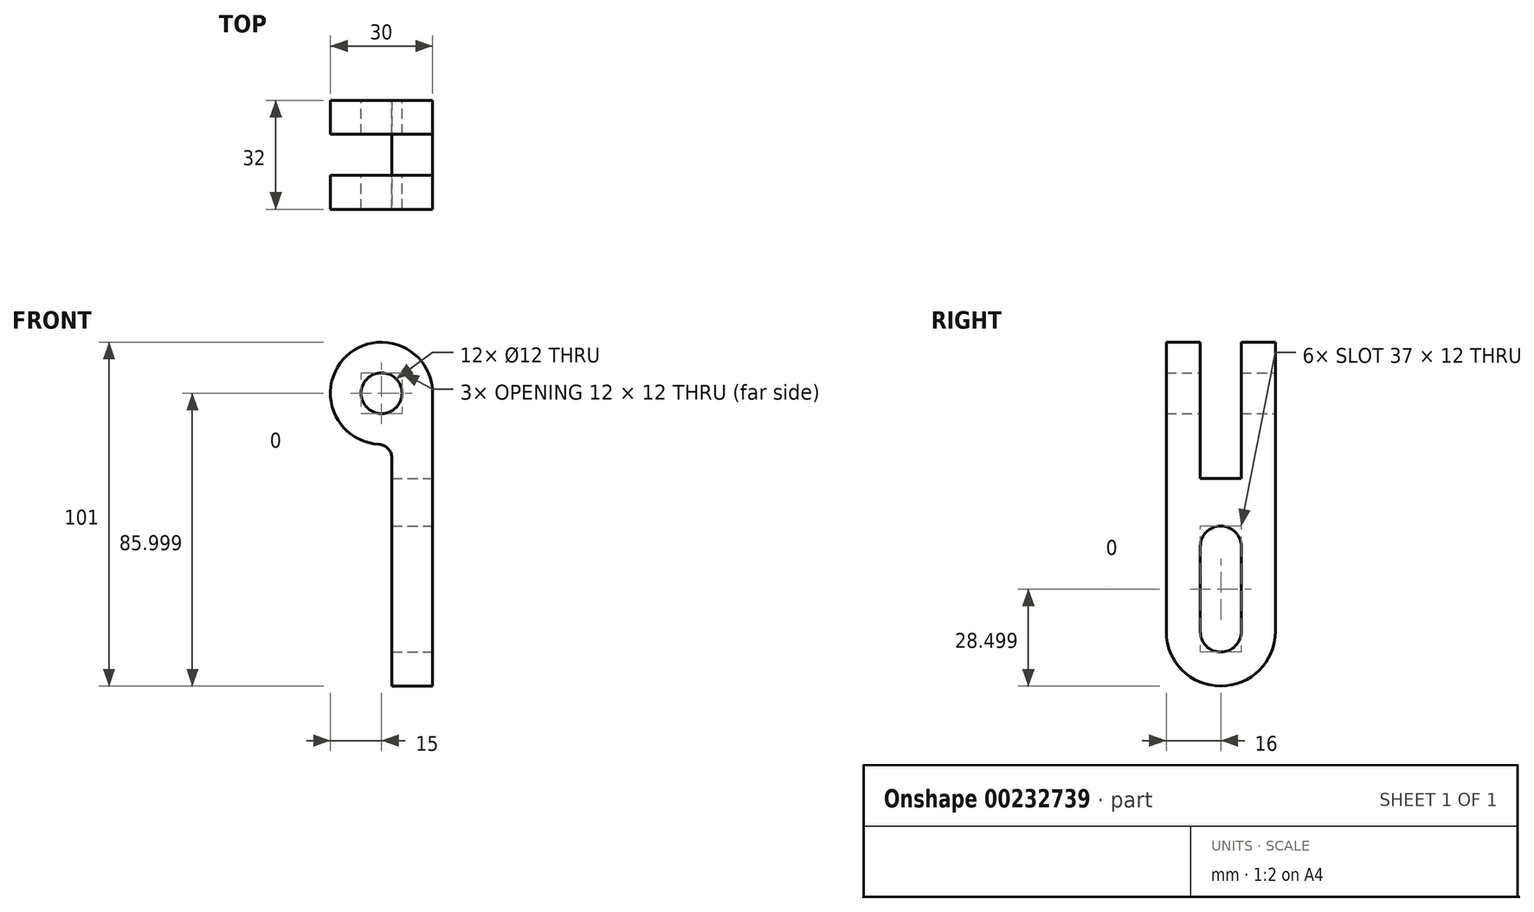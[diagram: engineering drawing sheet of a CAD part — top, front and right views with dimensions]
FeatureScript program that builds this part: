
annotation { "Feature Type Name" : "Feature", "Feature Type Description" : "" }
export const myFeature = defineFeature(function(context is Context, id is Id, definition is map)
    precondition{}
    {
        {
            var Q0;
            Q0=qCreatedBy(makeId("Front.planeOp"),FACE);
            var sketch = newSketch(context, id + "F0", { "sketchPlane" : qUnion([Q0])});
            skCircle(sketch, "E0", {"center": v(0, 39.04) * mm, "radius": 6 * mm});
            skArc(sketch, "E1", {"start": v(15, 39.04) * mm, "mid": v(-10.32, 49.92) * mm, "end": v(-0.79, 24.06) * mm});
            skLineSegment(sketch, "E2", {"start": v(15, 39.04) * mm, "end": v(15, -46.96) * mm});
            skLineSegment(sketch, "E3", {"start": v(15, -46.96) * mm, "end": v(3, -46.96) * mm});
            skLineSegment(sketch, "E4", {"start": v(3, -46.96) * mm, "end": v(3, 20.07) * mm});
            skPoint(sketch, "E5.visualSharp", {"position": v(3, 24.34) * mm});
            skArc(sketch, "E5.filletArc", {"start": v(3, 20.07) * mm, "mid": v(1.9, 22.82) * mm, "end": v(-0.79, 24.06) * mm});
            skSolve(sketch);
        }
        {
            var Q0;
            Q0=makeQuery(id+"F0.imprint","IMPRINT",FACE,{"disambiguationData":[TD([[makeQuery(id+"F0.imprint","IMPRINT",EDGE,{"derivedFrom":sQuery(id+"F0.wireOp",EDGE,"E0")}),-1.0]])]});
            extrude(context, id + "F1", {"entities" : qUnion([Q0]), "depth" : 32 * mm});
        }
        {
            var Q0;
            Q0=makeQuery(id+"F1.opExtrude","SWEPT_FACE",FACE,{"disambiguationData":[OSD([sQuery(id+"F0.wireOp",EDGE,"E2")])]});
            var sketch = newSketch(context, id + "F2", { "sketchPlane" : qUnion([Q0])});
            skArc(sketch, "E6", {"start": v(-32, -30.96) * mm, "mid": v(-16, -46.96) * mm, "end": v(0, -30.96) * mm});
            skArc(sketch, "E7", {"start": v(-22, -30.96) * mm, "mid": v(-16, -36.96) * mm, "end": v(-10, -30.96) * mm});
            skLineSegment(sketch, "E8", {"start": v(-32, -30.96) * mm, "end": v(0, -30.96) * mm, "construction": true});
            skLineSegment(sketch, "E9", {"start": v(-22, -5.96) * mm, "end": v(-22, -30.96) * mm});
            skLineSegment(sketch, "E10", {"start": v(-10, -5.96) * mm, "end": v(-10, -30.96) * mm});
            skLineSegment(sketch, "E11", {"start": v(-32, 33.86) * mm, "end": v(-32, 54.39) * mm});
            skLineSegment(sketch, "E12", {"start": v(-32, 54.39) * mm, "end": v(-22, 54.39) * mm});
            skLineSegment(sketch, "E13", {"start": v(-22, 54.39) * mm, "end": v(-22, 14.04) * mm});
            skLineSegment(sketch, "E14", {"start": v(-22, 14.04) * mm, "end": v(-10, 14.04) * mm});
            skLineSegment(sketch, "E15", {"start": v(-10, 14.04) * mm, "end": v(-10, 54.39) * mm});
            skLineSegment(sketch, "E16", {"start": v(-10, 54.39) * mm, "end": v(0, 54.39) * mm});
            skLineSegment(sketch, "E17", {"start": v(0, 54.39) * mm, "end": v(0, 29.64) * mm});
            skArc(sketch, "E18", {"start": v(-10, -5.96) * mm, "mid": v(-16, 0.04) * mm, "end": v(-22, -5.96) * mm});
            skLineSegment(sketch, "E19", {"start": v(-32, -30.96) * mm, "end": v(-32, -46.96) * mm, "construction": true});
            skLineSegment(sketch, "E20", {"start": v(-32, -46.96) * mm, "end": v(0, -46.96) * mm, "construction": true});
            skLineSegment(sketch, "E21", {"start": v(0, -46.96) * mm, "end": v(0, -30.96) * mm, "construction": true});
            skLineSegment(sketch, "E22", {"start": v(-22, 54.39) * mm, "end": v(-10, 54.39) * mm});
            skSolve(sketch);
        }
        {
            var Q0;
            {var subQ0=sQuery(id+"F2.wireOp",EDGE,"E22");Q0=makeQuery(id+"F2.imprint","IMPRINT",FACE,{"disambiguationData":[TD([[makeQuery(id+"F2.imprint","IMPRINT",EDGE,{"derivedFrom":subQ0}),-1.0]])]});}
            var Q1;
            {var subQ0=sQuery(id+"F2.wireOp",EDGE,"E14");Q1=makeQuery(id+"F2.imprint","IMPRINT",FACE,{"disambiguationData":[TD([[makeQuery(id+"F2.imprint","IMPRINT",EDGE,{"derivedFrom":subQ0}),1.0]])]});}
            var Q2;
            Q2=makeQuery(id+"F2.imprint","IMPRINT",FACE,{"disambiguationData":[TD([[makeQuery(id+"F2.imprint","IMPRINT",EDGE,{"derivedFrom":sQuery(id+"F2.wireOp",EDGE,"E7")}),1.0]])]});
            var Q3;
            {var subQ0=sQuery(id+"F2.wireOp",EDGE,"E6");var subQ1=sQuery(id+"F0.wireOp",EDGE,"E2");var subQ2=makeQuery(id+"F1.opExtrude","CAP_EDGE",EDGE,{"disambiguationData":[OSD([subQ1])],"isStart":false});var subQ3=makeQuery(id+"F2.imprint","INTERSECT",VERTEX,{"derivedFrom":[subQ2,subQ0,sQuery(id+"F2.wireOp",EDGE,"E11")]});Q3=makeQuery(id+"F2.imprint","IMPRINT",FACE,{"disambiguationData":[TD([[makeQuery(id+"F2.imprint","IMPRINT",EDGE,{"disambiguationData":[TD([[subQ3,-1.0]])],"derivedFrom":subQ0}),-1.0]])]});}
            var Q4;
            {var subQ0=sQuery(id+"F2.wireOp",EDGE,"E6");var subQ1=sQuery(id+"F0.wireOp",EDGE,"E2");var subQ2=makeQuery(id+"F1.opExtrude","CAP_EDGE",EDGE,{"disambiguationData":[OSD([subQ1])],"isStart":true});var subQ3=makeQuery(id+"F2.imprint","INTERSECT",VERTEX,{"derivedFrom":[subQ2,subQ0]});Q4=makeQuery(id+"F2.imprint","IMPRINT",FACE,{"disambiguationData":[TD([[makeQuery(id+"F2.imprint","IMPRINT",EDGE,{"disambiguationData":[TD([[subQ3,1.0]])],"derivedFrom":subQ0}),-1.0]])]});}
            extrude(context, id + "F3", {"entities" : qUnion([Q0, Q1, Q2, Q3, Q4]), "operationType" : NewBodyOperationType.REMOVE, "endBound" : BoundingType.THROUGH_ALL, "oppositeDirection" : true, "depth" : 25 * mm});
        }
    });
